# Revit family: Serene_T&T_Window_B_Standard
name_source: partatom
category: Windows
revit_build: Autodesk Revit 2014 (Build: 20130308_1515(x64)
units: mm (PartAtom-declared; Revit-internal decimal feet)

## types (18) — shared parameters
Centered In Wall = Yes
Custom Sash Width = 522 mm
DG Gasket Finish = Double Glazing Gasket Material
DG Gasket Tickness = 12 mm  [stored 0.0393701 ft]
DG Thickness Calc = 4 mm  [stored 0.0131234 ft]
Default Sill Height = 800 mm  [stored 2.62467 ft]
Description = Tilt and turn window, Type B
Frame Thickness = 52 mm
Frame Width = 62 mm  [stored 0.203412 ft]
Limit Fixed Pane Height Min = 200 mm  [stored 0.656168 ft]
Limit Fixed Panel Width Max = 1800 mm  [stored 5.90551 ft]
Limit Fixed Panel Width Min = 200 mm  [stored 0.656168 ft]
Limit Sash Height Max = 1500 mm  [stored 4.92126 ft]
Limit Sash Height Min = 300 mm  [stored 0.984252 ft]
Limit Sash Width Max = 700 mm  [stored 2.29659 ft]
Limit Sash Width Min = 300 mm  [stored 0.984252 ft]
Limit Window Height Max = 1568 mm  [stored 5.14436 ft]
Limit Window Height Min = 368 mm  [stored 1.20735 ft]
Limit Window Width Max = 2430 mm
Limit Window Width Min = 830 mm  [stored 2.7231 ft]
Manufacturer = Crealco
Max System DG One Piece Thickness = 4 mm  [stored 0.0131234 ft]
Max System DG Unit Thickness = 20 mm  [stored 0.0656168 ft]
Model = Serene
Sash Edge Gap = 34 mm
Sash Frame Gasket = 3 mm  [stored 0.00984252 ft]
Sash Overlap = 28 mm  [stored 0.0918635 ft]
Sash Width = 522 mm
URL = http://www.crealco.co.za
Wall Closure = By host
zero-valued in all types: Custom Window Exterior Offset

## per-type parameters (varying)
- 52TT-0909S-1500Pa: Area Glazing Fixed Panel=0.2 m²; Area Glazing Sash=0.3 m²; Clearvue Insulated LowE SHGC Value=0.382; Clearvue Insulated LowE U Value=4.3; Clearvue Insulated SHGC Value=0.419; Clearvue Insulated U Value=4.67; Clearvue SHGC Value=0.473; Clearvue U Value=6.38; Custom Windload=1500 mm  [stored 4.92126 ft]; Custom Window Height=890 mm  [stored 2.91995 ft]; Custom Window Width=890 mm  [stored 2.91995 ft]; Energy Advantage SHGC Value=0.425; Energy Advantage U Value=5.73; Fixed Panel Height=810 mm; Fixed Panel Width=260 mm  [stored 0.853018 ft]; Height=890 mm  [stored 2.91995 ft]; Intruderprufe LowE SHGC Value=0.389; Intruderprufe LowE U Value=4.68; Intruderprufe SHGC Value=0.439; Intruderprufe U Value=6.29; Length Mullion=810 mm; Max Pane Area=0.3 m²; Sash Height=822 mm  [stored 2.69685 ft]; Width=890 mm  [stored 2.91995 ft]; Windload Design=1500 mm  [stored 4.92126 ft]
- 52TT-0909S-2000Pa: Area Glazing Fixed Panel=0.2 m²; Area Glazing Sash=0.3 m²; Clearvue Insulated LowE SHGC Value=0.382; Clearvue Insulated LowE U Value=4.3; Clearvue Insulated SHGC Value=0.419; Clearvue Insulated U Value=4.67; Clearvue SHGC Value=0.473; Clearvue U Value=6.38; Custom Windload=2000 mm  [stored 6.56168 ft]; Custom Window Height=890 mm  [stored 2.91995 ft]; Custom Window Width=890 mm  [stored 2.91995 ft]; Energy Advantage SHGC Value=0.425; Energy Advantage U Value=5.73; Fixed Panel Height=810 mm; Fixed Panel Width=260 mm  [stored 0.853018 ft]; Height=890 mm  [stored 2.91995 ft]; Intruderprufe LowE SHGC Value=0.389; Intruderprufe LowE U Value=4.68; Intruderprufe SHGC Value=0.439; Intruderprufe U Value=6.29; Length Mullion=810 mm; Max Pane Area=0.3 m²; Sash Height=822 mm  [stored 2.69685 ft]; Width=890 mm  [stored 2.91995 ft]; Windload Design=2000 mm  [stored 6.56168 ft]
- 52TT-1209S-1000Pa: Area Glazing Fixed Panel=0.44 m²; Area Glazing Sash=0.3 m²; Clearvue Insulated LowE SHGC Value=0.433; Clearvue Insulated LowE U Value=3.88; Clearvue Insulated SHGC Value=0.475; Clearvue Insulated U Value=4.33; Clearvue SHGC Value=0.539; Clearvue U Value=6.27; Custom Windload=1000 mm  [stored 3.28084 ft]; Custom Window Height=890 mm  [stored 2.91995 ft]; Custom Window Width=1190 mm  [stored 3.9042 ft]; Energy Advantage SHGC Value=0.483; Energy Advantage U Value=5.4; Fixed Panel Height=810 mm; Fixed Panel Width=560 mm; Height=890 mm  [stored 2.91995 ft]; Intruderprufe LowE SHGC Value=0.441; Intruderprufe LowE U Value=4.58; Intruderprufe SHGC Value=0.498; Intruderprufe U Value=6.16; Length Mullion=810 mm; Max Pane Area=0.44 m²; Sash Height=822 mm  [stored 2.69685 ft]; Width=1190 mm  [stored 3.9042 ft]; Windload Design=1000 mm  [stored 3.28084 ft]
- 52TT-1209S-1500Pa: Area Glazing Fixed Panel=0.44 m²; Area Glazing Sash=0.3 m²; Clearvue Insulated LowE SHGC Value=0.433; Clearvue Insulated LowE U Value=3.88; Clearvue Insulated SHGC Value=0.475; Clearvue Insulated U Value=4.33; Clearvue SHGC Value=0.539; Clearvue U Value=6.27; Custom Windload=1500 mm  [stored 4.92126 ft]; Custom Window Height=890 mm  [stored 2.91995 ft]; Custom Window Width=1190 mm  [stored 3.9042 ft]; Energy Advantage SHGC Value=0.483; Energy Advantage U Value=5.4; Fixed Panel Height=810 mm; Fixed Panel Width=560 mm; Height=890 mm  [stored 2.91995 ft]; Intruderprufe LowE SHGC Value=0.441; Intruderprufe LowE U Value=4.58; Intruderprufe SHGC Value=0.498; Intruderprufe U Value=6.16; Length Mullion=810 mm; Max Pane Area=0.44 m²; Sash Height=822 mm  [stored 2.69685 ft]; Width=1190 mm  [stored 3.9042 ft]; Windload Design=1500 mm  [stored 4.92126 ft]
- 52TT-1209S-2000Pa: Area Glazing Fixed Panel=0.44 m²; Area Glazing Sash=0.3 m²; Clearvue Insulated LowE SHGC Value=0.433; Clearvue Insulated LowE U Value=3.88; Clearvue Insulated SHGC Value=0.475; Clearvue Insulated U Value=4.33; Clearvue SHGC Value=0.539; Clearvue U Value=6.27; Custom Windload=2000 mm  [stored 6.56168 ft]; Custom Window Height=890 mm  [stored 2.91995 ft]; Custom Window Width=1190 mm  [stored 3.9042 ft]; Energy Advantage SHGC Value=0.483; Energy Advantage U Value=5.4; Fixed Panel Height=810 mm; Fixed Panel Width=560 mm; Height=890 mm  [stored 2.91995 ft]; Intruderprufe LowE SHGC Value=0.441; Intruderprufe LowE U Value=4.58; Intruderprufe SHGC Value=0.498; Intruderprufe U Value=6.16; Length Mullion=810 mm; Max Pane Area=0.44 m²; Sash Height=822 mm  [stored 2.69685 ft]; Width=1190 mm  [stored 3.9042 ft]; Windload Design=2000 mm  [stored 6.56168 ft]
- 52TT-1509S-1000Pa: Area Glazing Fixed Panel=0.68 m²; Area Glazing Sash=0.3 m²; Clearvue Insulated LowE SHGC Value=0.464; Clearvue Insulated LowE U Value=3.63; Clearvue Insulated SHGC Value=0.509; Clearvue Insulated U Value=4.12; Clearvue SHGC Value=0.577; Clearvue U Value=6.21; Custom Windload=1000 mm  [stored 3.28084 ft]; Custom Window Height=890 mm  [stored 2.91995 ft]; Custom Window Width=1490 mm  [stored 4.88845 ft]; Energy Advantage SHGC Value=0.517; Energy Advantage U Value=5.2; Fixed Panel Height=810 mm; Fixed Panel Width=860 mm  [stored 2.82152 ft]; Height=890 mm  [stored 2.91995 ft]; Intruderprufe LowE SHGC Value=0.473; Intruderprufe LowE U Value=4.53; Intruderprufe SHGC Value=0.534; Intruderprufe U Value=6.09; Length Mullion=810 mm; Max Pane Area=0.68 m²; Sash Height=822 mm  [stored 2.69685 ft]; Width=1490 mm  [stored 4.88845 ft]; Windload Design=1000 mm  [stored 3.28084 ft]
- 52TT-1509S-1500Pa: Area Glazing Fixed Panel=0.68 m²; Area Glazing Sash=0.3 m²; Clearvue Insulated LowE SHGC Value=0.464; Clearvue Insulated LowE U Value=3.63; Clearvue Insulated SHGC Value=0.509; Clearvue Insulated U Value=4.12; Clearvue SHGC Value=0.577; Clearvue U Value=6.21; Custom Windload=1500 mm  [stored 4.92126 ft]; Custom Window Height=890 mm  [stored 2.91995 ft]; Custom Window Width=1490 mm  [stored 4.88845 ft]; Energy Advantage SHGC Value=0.517; Energy Advantage U Value=5.2; Fixed Panel Height=810 mm; Fixed Panel Width=860 mm  [stored 2.82152 ft]; Height=890 mm  [stored 2.91995 ft]; Intruderprufe LowE SHGC Value=0.473; Intruderprufe LowE U Value=4.53; Intruderprufe SHGC Value=0.534; Intruderprufe U Value=6.09; Length Mullion=810 mm; Max Pane Area=0.68 m²; Sash Height=822 mm  [stored 2.69685 ft]; Width=1490 mm  [stored 4.88845 ft]; Windload Design=1500 mm  [stored 4.92126 ft]
- 52TT-1509S-2000Pa: Area Glazing Fixed Panel=0.68 m²; Area Glazing Sash=0.3 m²; Clearvue Insulated LowE SHGC Value=0.464; Clearvue Insulated LowE U Value=3.63; Clearvue Insulated SHGC Value=0.509; Clearvue Insulated U Value=4.12; Clearvue SHGC Value=0.577; Clearvue U Value=6.21; Custom Windload=2000 mm  [stored 6.56168 ft]; Custom Window Height=890 mm  [stored 2.91995 ft]; Custom Window Width=1490 mm  [stored 4.88845 ft]; Energy Advantage SHGC Value=0.517; Energy Advantage U Value=5.2; Fixed Panel Height=810 mm; Fixed Panel Width=860 mm  [stored 2.82152 ft]; Height=890 mm  [stored 2.91995 ft]; Intruderprufe LowE SHGC Value=0.473; Intruderprufe LowE U Value=4.53; Intruderprufe SHGC Value=0.534; Intruderprufe U Value=6.09; Length Mullion=810 mm; Max Pane Area=0.68 m²; Sash Height=822 mm  [stored 2.69685 ft]; Width=1490 mm  [stored 4.88845 ft]; Windload Design=2000 mm  [stored 6.56168 ft]
- 52TT-0912S-1000Pa: Area Glazing Fixed Panel=0.28 m²; Area Glazing Sash=0.43 m²; Clearvue Insulated LowE SHGC Value=0.403; Clearvue Insulated LowE U Value=4.13; Clearvue Insulated SHGC Value=0.441; Clearvue Insulated U Value=4.53; Clearvue SHGC Value=0.499; Clearvue U Value=6.32; Custom Windload=1000 mm  [stored 3.28084 ft]; Custom Window Height=1190 mm  [stored 3.9042 ft]; Custom Window Width=890 mm  [stored 2.91995 ft]; Energy Advantage SHGC Value=0.449; Energy Advantage U Value=5.61; Fixed Panel Height=1110 mm; Fixed Panel Width=260 mm  [stored 0.853018 ft]; Height=1190 mm  [stored 3.9042 ft]; Intruderprufe LowE SHGC Value=0.41; Intruderprufe LowE U Value=4.63; Intruderprufe SHGC Value=0.463; Intruderprufe U Value=6.23; Length Mullion=1110 mm; Max Pane Area=0.43 m²; Sash Height=1122 mm  [stored 3.6811 ft]; Width=890 mm  [stored 2.91995 ft]; Windload Design=1000 mm  [stored 3.28084 ft]
- 52TT-0912S-1500Pa: Area Glazing Fixed Panel=0.28 m²; Area Glazing Sash=0.43 m²; Clearvue Insulated LowE SHGC Value=0.403; Clearvue Insulated LowE U Value=4.13; Clearvue Insulated SHGC Value=0.441; Clearvue Insulated U Value=4.53; Clearvue SHGC Value=0.499; Clearvue U Value=6.32; Custom Windload=1500 mm  [stored 4.92126 ft]; Custom Window Height=1190 mm  [stored 3.9042 ft]; Custom Window Width=890 mm  [stored 2.91995 ft]; Energy Advantage SHGC Value=0.449; Energy Advantage U Value=5.61; Fixed Panel Height=1110 mm; Fixed Panel Width=260 mm  [stored 0.853018 ft]; Height=1190 mm  [stored 3.9042 ft]; Intruderprufe LowE SHGC Value=0.41; Intruderprufe LowE U Value=4.63; Intruderprufe SHGC Value=0.463; Intruderprufe U Value=6.23; Length Mullion=1110 mm; Max Pane Area=0.43 m²; Sash Height=1122 mm  [stored 3.6811 ft]; Width=890 mm  [stored 2.91995 ft]; Windload Design=1500 mm  [stored 4.92126 ft]
- 52TT-0912S-2000Pa: Area Glazing Fixed Panel=0.28 m²; Area Glazing Sash=0.43 m²; Clearvue Insulated LowE SHGC Value=0.403; Clearvue Insulated LowE U Value=4.13; Clearvue Insulated SHGC Value=0.441; Clearvue Insulated U Value=4.53; Clearvue SHGC Value=0.499; Clearvue U Value=6.32; Custom Windload=2000 mm  [stored 6.56168 ft]; Custom Window Height=1190 mm  [stored 3.9042 ft]; Custom Window Width=890 mm  [stored 2.91995 ft]; Energy Advantage SHGC Value=0.449; Energy Advantage U Value=5.61; Fixed Panel Height=1110 mm; Fixed Panel Width=260 mm  [stored 0.853018 ft]; Height=1190 mm  [stored 3.9042 ft]; Intruderprufe LowE SHGC Value=0.41; Intruderprufe LowE U Value=4.63; Intruderprufe SHGC Value=0.463; Intruderprufe U Value=6.23; Length Mullion=1110 mm; Max Pane Area=0.43 m²; Sash Height=1122 mm  [stored 3.6811 ft]; Width=890 mm  [stored 2.91995 ft]; Windload Design=2000 mm  [stored 6.56168 ft]
- 52TT-1212S-1000Pa: Area Glazing Fixed Panel=0.61 m²; Area Glazing Sash=0.43 m²; Clearvue Insulated LowE SHGC Value=0.455; Clearvue Insulated LowE U Value=3.71; Clearvue Insulated SHGC Value=0.499; Clearvue Insulated U Value=4.19; Clearvue SHGC Value=0.565; Clearvue U Value=6.22; Custom Windload=1000 mm  [stored 3.28084 ft]; Custom Window Height=1190 mm  [stored 3.9042 ft]; Custom Window Width=1190 mm  [stored 3.9042 ft]; Energy Advantage SHGC Value=0.507; Energy Advantage U Value=5.26; Fixed Panel Height=1110 mm; Fixed Panel Width=560 mm; Height=1190 mm  [stored 3.9042 ft]; Intruderprufe LowE SHGC Value=0.464; Intruderprufe LowE U Value=4.54; Intruderprufe SHGC Value=0.523; Intruderprufe U Value=6.11; Length Mullion=1110 mm; Max Pane Area=0.61 m²; Sash Height=1122 mm  [stored 3.6811 ft]; Width=1190 mm  [stored 3.9042 ft]; Windload Design=1000 mm  [stored 3.28084 ft]
- 52TT-1212S-1500Pa: Area Glazing Fixed Panel=0.61 m²; Area Glazing Sash=0.43 m²; Clearvue Insulated LowE SHGC Value=0.455; Clearvue Insulated LowE U Value=3.71; Clearvue Insulated SHGC Value=0.499; Clearvue Insulated U Value=4.19; Clearvue SHGC Value=0.565; Clearvue U Value=6.22; Custom Windload=1500 mm  [stored 4.92126 ft]; Custom Window Height=1190 mm  [stored 3.9042 ft]; Custom Window Width=1190 mm  [stored 3.9042 ft]; Energy Advantage SHGC Value=0.507; Energy Advantage U Value=5.26; Fixed Panel Height=1110 mm; Fixed Panel Width=560 mm; Height=1190 mm  [stored 3.9042 ft]; Intruderprufe LowE SHGC Value=0.464; Intruderprufe LowE U Value=4.54; Intruderprufe SHGC Value=0.523; Intruderprufe U Value=6.11; Length Mullion=1110 mm; Max Pane Area=0.61 m²; Sash Height=1122 mm  [stored 3.6811 ft]; Width=1190 mm  [stored 3.9042 ft]; Windload Design=1500 mm  [stored 4.92126 ft]
- 52TT-1212S-2000Pa: Area Glazing Fixed Panel=0.61 m²; Area Glazing Sash=0.43 m²; Clearvue Insulated LowE SHGC Value=0.455; Clearvue Insulated LowE U Value=3.71; Clearvue Insulated SHGC Value=0.499; Clearvue Insulated U Value=4.19; Clearvue SHGC Value=0.565; Clearvue U Value=6.22; Custom Windload=2000 mm  [stored 6.56168 ft]; Custom Window Height=1190 mm  [stored 3.9042 ft]; Custom Window Width=1190 mm  [stored 3.9042 ft]; Energy Advantage SHGC Value=0.507; Energy Advantage U Value=5.26; Fixed Panel Height=1110 mm; Fixed Panel Width=560 mm; Height=1190 mm  [stored 3.9042 ft]; Intruderprufe LowE SHGC Value=0.464; Intruderprufe LowE U Value=4.54; Intruderprufe SHGC Value=0.523; Intruderprufe U Value=6.11; Length Mullion=1110 mm; Max Pane Area=0.61 m²; Sash Height=1122 mm  [stored 3.6811 ft]; Width=1190 mm  [stored 3.9042 ft]; Windload Design=2000 mm  [stored 6.56168 ft]
- 52TT-1512S-1000Pa: Area Glazing Fixed Panel=0.94 m²; Area Glazing Sash=0.43 m²; Clearvue Insulated LowE SHGC Value=0.486; Clearvue Insulated LowE U Value=3.46; Clearvue Insulated SHGC Value=0.533; Clearvue Insulated U Value=3.98; Clearvue SHGC Value=0.605; Clearvue U Value=6.17; Custom Windload=1000 mm  [stored 3.28084 ft]; Custom Window Height=1190 mm  [stored 3.9042 ft]; Custom Window Width=1490 mm  [stored 4.88845 ft]; Energy Advantage SHGC Value=0.542; Energy Advantage U Value=5.06; Fixed Panel Height=1110 mm; Fixed Panel Width=860 mm  [stored 2.82152 ft]; Height=1190 mm  [stored 3.9042 ft]; Intruderprufe LowE SHGC Value=0.496; Intruderprufe LowE U Value=4.49; Intruderprufe SHGC Value=0.559; Intruderprufe U Value=6.04; Length Mullion=1110 mm; Max Pane Area=0.94 m²; Sash Height=1122 mm  [stored 3.6811 ft]; Width=1490 mm  [stored 4.88845 ft]; Windload Design=1000 mm  [stored 3.28084 ft]
- 52TT-1512S-1500Pa: Area Glazing Fixed Panel=0.94 m²; Area Glazing Sash=0.43 m²; Clearvue Insulated LowE SHGC Value=0.486; Clearvue Insulated LowE U Value=3.46; Clearvue Insulated SHGC Value=0.533; Clearvue Insulated U Value=3.98; Clearvue SHGC Value=0.605; Clearvue U Value=6.17; Custom Windload=1500 mm  [stored 4.92126 ft]; Custom Window Height=1190 mm  [stored 3.9042 ft]; Custom Window Width=1490 mm  [stored 4.88845 ft]; Energy Advantage SHGC Value=0.542; Energy Advantage U Value=5.06; Fixed Panel Height=1110 mm; Fixed Panel Width=860 mm  [stored 2.82152 ft]; Height=1190 mm  [stored 3.9042 ft]; Intruderprufe LowE SHGC Value=0.496; Intruderprufe LowE U Value=4.49; Intruderprufe SHGC Value=0.559; Intruderprufe U Value=6.04; Length Mullion=1110 mm; Max Pane Area=0.94 m²; Sash Height=1122 mm  [stored 3.6811 ft]; Width=1490 mm  [stored 4.88845 ft]; Windload Design=1500 mm  [stored 4.92126 ft]
- 52TT-1512S-2000Pa: Area Glazing Fixed Panel=0.94 m²; Area Glazing Sash=0.43 m²; Clearvue Insulated LowE SHGC Value=0.486; Clearvue Insulated LowE U Value=3.46; Clearvue Insulated SHGC Value=0.533; Clearvue Insulated U Value=3.98; Clearvue SHGC Value=0.605; Clearvue U Value=6.17; Custom Windload=2000 mm  [stored 6.56168 ft]; Custom Window Height=1190 mm  [stored 3.9042 ft]; Custom Window Width=1490 mm  [stored 4.88845 ft]; Energy Advantage SHGC Value=0.542; Energy Advantage U Value=5.06; Fixed Panel Height=1110 mm; Fixed Panel Width=860 mm  [stored 2.82152 ft]; Height=1190 mm  [stored 3.9042 ft]; Intruderprufe LowE SHGC Value=0.496; Intruderprufe LowE U Value=4.49; Intruderprufe SHGC Value=0.559; Intruderprufe U Value=6.04; Length Mullion=1110 mm; Max Pane Area=0.94 m²; Sash Height=1122 mm  [stored 3.6811 ft]; Width=1490 mm  [stored 4.88845 ft]; Windload Design=2000 mm  [stored 6.56168 ft]
- 52TT-0909S-1000Pa: Area Glazing Fixed Panel=0.2 m²; Area Glazing Sash=0.3 m²; Clearvue Insulated LowE SHGC Value=0.382; Clearvue Insulated LowE U Value=4.3; Clearvue Insulated SHGC Value=0.419; Clearvue Insulated U Value=4.67; Clearvue SHGC Value=0.473; Clearvue U Value=6.38; Custom Windload=1000 mm  [stored 3.28084 ft]; Custom Window Height=890 mm  [stored 2.91995 ft]; Custom Window Width=890 mm  [stored 2.91995 ft]; Energy Advantage SHGC Value=0.425; Energy Advantage U Value=5.73; Fixed Panel Height=810 mm; Fixed Panel Width=260 mm  [stored 0.853018 ft]; Height=890 mm  [stored 2.91995 ft]; Intruderprufe LowE SHGC Value=0.389; Intruderprufe LowE U Value=4.68; Intruderprufe SHGC Value=0.439; Intruderprufe U Value=6.29; Length Mullion=810 mm; Max Pane Area=0.3 m²; Sash Height=822 mm  [stored 2.69685 ft]; Width=890 mm  [stored 2.91995 ft]; Windload Design=1000 mm  [stored 3.28084 ft]

note: [stored X ft] marks values corroborated as IEEE doubles in the binary element streams (Revit-internal decimal feet)

## geometry (parser evidence)
native form markers: Sweep x28
no freeform markers — native parametric forms only
